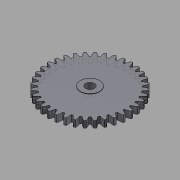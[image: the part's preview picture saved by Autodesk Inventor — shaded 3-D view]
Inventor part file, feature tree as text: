
AUTODESK INVENTOR PART (.ipt)
format: ipt  version: 2015 (Build 190159000, 159)  size: 285,696 bytes
history: native  units: mm (DEFAULTED — no unit token found)
features: sketch x4, extrude x3, plane x3, other x3
ambient origin geometry x8: Origin, YZ Plane, XZ Plane, XY Plane, X Axis, Y Axis, Z Axis, Center Point
bodies: Solid1 (feature_tree)
feature tree (13):
  extrude  "Extrusion1"  Depth=1.5mm TaperAngle=0.0deg
  plane  "Work Plane2"
  plane  "Work Plane8"
  plane  "Work Plane9"
  other  "Spur Gear"
  extrude  "Extrusion2"  Depth=10.0mm TaperAngle=0.0deg
  extrude  "Extrusion3"  Depth=0.872665mm TaperAngle=0.0deg
  sketch  "Sketch1"  dims[d0=19.0mm d1=1.5mm d2=0.0mm]
  sketch  "Sketch2"  dims[d3=18.0mm d4=10.0mm d5=0.0mm]
  other  "Srf1"
  sketch  "Sketch3"  dims[d16=11.5mm d17=0.0mm d34=0.872665mm]
  sketch  "Sketch4"  dims[d39=0.0mm d41=0.0mm d43=11.5mm d46=11.5mm d47=0.0mm d48=0.0mm d49=4.3mm d50=0.1mm d51=0.0mm d52=2.0mm d53=0.1mm d54=0.0mm]
  other  "Pitch Diameter"
